# Revit family: CENTUM Doppel-Rollenlager, radial- axial
name_source: partatom
category: HLS-Bauteile
revit_build: Autodesk Revit 2017 (Build: 20190507_1515(x64)
units: mm (PartAtom-declared; Revit-internal decimal feet)

## family parameters
Arbeitsebenenbasiert = Ja
Beim Laden mit Abzugskörper schneiden = Nein
Bemaßung runder Anschluss = Durchmesser verwenden
Gemeinsam genutzt = Ja
Immer vertikal = Nein
Raumberechnungspunkt = Nein
Teiletyp = Normal

## types (117) — shared parameters
Fabrikat = MEFA
Firma = MEFA Befestigungs- und Montagesysteme GmbH
Kurztext1 = Rollenlager doppel radial-axial
Material = Stahl
Materialname = S235
Mengeneinheit = St
Vorgabe-Ansicht = 1219 mm
vpe = 1 St
zero-valued in all types: Sicherheitsfaktor

## per-type parameters (varying)
| type | Artikelnummer | Breite mit Laschen | Doppel-Rollenlager, ra-ax | EAN | Gewicht | Gewicht pro Bauteil | Höhe | Kurztext2 | Langloch | Lasttyp | Lochabstand längs | Lochabstand quer | Länge | Oberflaeche | Schiebeweg | Stärke Material | max. Auflagenbreite | max. zul. Last | min. Auflagenbreite |
| Doppel-Rollenlager, radial- axial  114- 273 DRX003 L= 100, fvz | 150xfa030273 | 232 mm | MEFA Doppel-Rollenlager, radial- axial  114- 273 DRX003 L= 100 | 4250928435460 | 8.62 kg | 8.62 kg | 76 mm | 114 - 273 mm 3 kN 100 mm fsv | 14x27 mm | DRX 003 | 180 mm  [stored 0.590551 ft] | 204 mm | 320 mm  [stored 1.04987 ft] | feuerstückverzinkt | 100 mm | 3 mm  [stored 0.00984252 ft] | 273 mm | 3.00 kN | 114 mm |
| Doppel-Rollenlager, radial- axial  219- 406 DRX005 L= 100, fvz | 150xfa040406 | 244 mm | MEFA Doppel-Rollenlager, radial- axial  219- 406 DRX005 L= 100 | 4250928435477 | 11.26 kg | 11.26 kg | 86 mm | 219 - 406 mm 5 kN 100 mm fsv | 14x27 mm | DRX 005 | 230 mm  [stored 0.754593 ft] | 216 mm  [stored 0.708661 ft] | 370 mm  [stored 1.21391 ft] | feuerstückverzinkt | 100 mm | 4 mm  [stored 0.0131234 ft] | 406 mm | 5.00 kN | 219 mm |
| Doppel-Rollenlager, radial- axial  114- 273 DRX003 L= 100, gvz | 150xga030273 | 232 mm | MEFA Doppel-Rollenlager, radial- axial  114- 273 DRX003 L= 100 | 4250928435859 | 8.26 kg | 8.26 kg | 76 mm | 114 - 273 mm 3 kN 100 mm gvz | 14x27 mm | DRX 003 | 180 mm  [stored 0.590551 ft] | 204 mm | 320 mm  [stored 1.04987 ft] | galvanisch verzinkt | 100 mm | 3 mm  [stored 0.00984252 ft] | 273 mm | 3.00 kN | 114 mm |
| Doppel-Rollenlager, radial- axial  114- 273 DRX003 L= 100, roh | 150xra030273 | 232 mm | MEFA Doppel-Rollenlager, radial- axial  114- 273 DRX003 L= 100 | 4250928436245 | 8.26 kg | 8.26 kg | 76 mm | 114 - 273 mm 3 kN 100 mm roh | 14x27 mm | DRX 003 | 180 mm  [stored 0.590551 ft] | 204 mm | 320 mm  [stored 1.04987 ft] | roh | 100 mm | 3 mm  [stored 0.00984252 ft] | 273 mm | 3.00 kN | 114 mm |
| Doppel-Rollenlager, radial- axial  219- 406 DRX005 L= 100, gvz | 150xga040406 | 244 mm | MEFA Doppel-Rollenlager, radial- axial  219- 406 DRX005 L= 100 | 4250928435866 | 10.83 kg | 10.83 kg | 86 mm | 219 - 406 mm 5 kN 100 mm gvz | 14x27 mm | DRX 005 | 230 mm  [stored 0.754593 ft] | 216 mm  [stored 0.708661 ft] | 370 mm  [stored 1.21391 ft] | galvanisch verzinkt | 100 mm | 4 mm  [stored 0.0131234 ft] | 406 mm | 5.00 kN | 219 mm |
| Doppel-Rollenlager, radial- axial  219- 406 DRX005 L= 100, roh | 150xra040406 | 244 mm | MEFA Doppel-Rollenlager, radial- axial  219- 406 DRX005 L= 100 | 4250928436252 | 10.83 kg | 10.83 kg | 86 mm | 219 - 406 mm 5 kN 100 mm roh | 14x27 mm | DRX 005 | 230 mm  [stored 0.754593 ft] | 216 mm  [stored 0.708661 ft] | 370 mm  [stored 1.21391 ft] | roh | 100 mm | 4 mm  [stored 0.0131234 ft] | 406 mm | 5.00 kN | 219 mm |
| Doppel-Rollenlager, radial- axial  114- 273 DRX003 L= 200, fvz | 150xfb030273 | 232 mm | MEFA Doppel-Rollenlager, radial- axial  114- 273 DRX003 L= 200 | 4250928435590 | 9.85 kg | 9.85 kg | 76 mm | 114 - 273 mm 3 kN 200 mm fsv | 14x27 mm | DRX 003 | 280 mm  [stored 0.918635 ft] | 204 mm | 420 mm  [stored 1.37795 ft] | feuerstückverzinkt | 200 mm | 3 mm  [stored 0.00984252 ft] | 273 mm | 3.00 kN | 114 mm |
| Doppel-Rollenlager, radial- axial  114- 273 DRX003 L= 200, gvz | 150xgb030273 | 232 mm | MEFA Doppel-Rollenlager, radial- axial  114- 273 DRX003 L= 200 | 4250928435989 | 9.10 kg | 9.10 kg | 76 mm | 114 - 273 mm 3 kN 200 mm gvz | 14x27 mm | DRX 003 | 280 mm  [stored 0.918635 ft] | 204 mm | 420 mm  [stored 1.37795 ft] | galvanisch verzinkt | 200 mm | 3 mm  [stored 0.00984252 ft] | 273 mm | 3.00 kN | 114 mm |
| Doppel-Rollenlager, radial- axial  114- 273 DRX003 L= 200, roh | 150xrb030273 | 232 mm | MEFA Doppel-Rollenlager, radial- axial  114- 273 DRX003 L= 200 | 4250928436375 | 9.43 kg | 9.43 kg | 76 mm | 114 - 273 mm 3 kN 200 mm roh | 14x27 mm | DRX 003 | 280 mm  [stored 0.918635 ft] | 204 mm | 420 mm  [stored 1.37795 ft] | roh | 200 mm | 3 mm  [stored 0.00984252 ft] | 273 mm | 3.00 kN | 114 mm |
| Doppel-Rollenlager, radial- axial  114- 273 DRX003 L= 300, fvz | 150xfc030273 | 232 mm | MEFA Doppel-Rollenlager, radial- axial  114- 273 DRX003 L= 300 | 4250928435729 | 11.09 kg | 11.09 kg | 76 mm | 114 - 273 mm 3 kN 300 mm fsv | 14x27 mm | DRX 003 | 380 mm | 204 mm | 520 mm  [stored 1.70604 ft] | feuerstückverzinkt | 300 mm | 3 mm  [stored 0.00984252 ft] | 273 mm | 3.00 kN | 114 mm |
| Doppel-Rollenlager, radial- axial  114- 273 DRX003 L= 300, gvz | 150xgc030273 | 232 mm | MEFA Doppel-Rollenlager, radial- axial  114- 273 DRX003 L= 300 | 4250928436115 | 10.20 kg | 10.20 kg | 76 mm | 114 - 273 mm 3 kN 300 mm gvz | 14x27 mm | DRX 003 | 380 mm | 204 mm | 520 mm  [stored 1.70604 ft] | galvanisch verzinkt | 300 mm | 3 mm  [stored 0.00984252 ft] | 273 mm | 3.00 kN | 114 mm |
| Doppel-Rollenlager, radial- axial  114- 273 DRX003 L= 300, roh | 150xrc030273 | 232 mm | MEFA Doppel-Rollenlager, radial- axial  114- 273 DRX003 L= 300 | 4250928436504 | 10.61 kg | 10.61 kg | 76 mm | 114 - 273 mm 3 kN 300 mm roh | 14x27 mm | DRX 003 | 380 mm | 204 mm | 520 mm  [stored 1.70604 ft] | roh | 300 mm | 3 mm  [stored 0.00984252 ft] | 273 mm | 3.00 kN | 114 mm |
| Doppel-Rollenlager, radial- axial  219- 406 DRX005 L= 200, fvz | 150xfb040406 | 244 mm | MEFA Doppel-Rollenlager, radial- axial  219- 406 DRX005 L= 200 | 4250928435606 | 12.50 kg | 12.50 kg | 86 mm | 219 - 406 mm 5 kN 200 mm fsv | 14x27 mm | DRX 005 | 330 mm | 216 mm  [stored 0.708661 ft] | 470 mm  [stored 1.54199 ft] | feuerstückverzinkt | 200 mm | 4 mm  [stored 0.0131234 ft] | 406 mm | 5.00 kN | 219 mm |
| Doppel-Rollenlager, radial- axial  219- 406 DRX005 L= 200, gvz | 150xgb040406 | 244 mm | MEFA Doppel-Rollenlager, radial- axial  219- 406 DRX005 L= 200 | 4250928435996 | 11.60 kg | 11.60 kg | 86 mm | 219 - 406 mm 5 kN 200 mm gvz | 14x27 mm | DRX 005 | 330 mm | 216 mm  [stored 0.708661 ft] | 470 mm  [stored 1.54199 ft] | galvanisch verzinkt | 200 mm | 4 mm  [stored 0.0131234 ft] | 406 mm | 5.00 kN | 219 mm |
| Doppel-Rollenlager, radial- axial  219- 406 DRX005 L= 200, roh | 150xrb040406 | 244 mm | MEFA Doppel-Rollenlager, radial- axial  219- 406 DRX005 L= 200 | 4250928436382 | 12.00 kg | 12.00 kg | 86 mm | 219 - 406 mm 5 kN 200 mm roh | 14x27 mm | DRX 005 | 330 mm | 216 mm  [stored 0.708661 ft] | 470 mm  [stored 1.54199 ft] | roh | 200 mm | 4 mm  [stored 0.0131234 ft] | 406 mm | 5.00 kN | 219 mm |
| Doppel-Rollenlager, radial- axial  219- 406 DRX005 L= 300, fvz | 150xfc040406 | 244 mm | MEFA Doppel-Rollenlager, radial- axial  219- 406 DRX005 L= 300 | 4250928435736 | 13.74 kg | 13.74 kg | 86 mm | 219 - 406 mm 5 kN 300 mm fsv | 14x27 mm | DRX 005 | 430 mm | 216 mm  [stored 0.708661 ft] | 570 mm  [stored 1.87008 ft] | feuerstückverzinkt | 300 mm | 4 mm  [stored 0.0131234 ft] | 406 mm | 5.00 kN | 219 mm |
| Doppel-Rollenlager, radial- axial  219- 406 DRX005 L= 300, gvz | 150xgc040406 | 244 mm | MEFA Doppel-Rollenlager, radial- axial  219- 406 DRX005 L= 300 | 4250928436122 | 12.70 kg | 12.70 kg | 86 mm | 219 - 406 mm 5 kN 300 mm gvz | 14x27 mm | DRX 005 | 430 mm | 216 mm  [stored 0.708661 ft] | 570 mm  [stored 1.87008 ft] | galvanisch verzinkt | 300 mm | 4 mm  [stored 0.0131234 ft] | 406 mm | 5.00 kN | 219 mm |
| Doppel-Rollenlager, radial- axial  219- 406 DRX005 L= 300, roh | 150xrc040406 | 244 mm | MEFA Doppel-Rollenlager, radial- axial  219- 406 DRX005 L= 300 | 4250928436511 | 13.18 kg | 13.18 kg | 86 mm | 219 - 406 mm 5 kN 300 mm roh | 14x27 mm | DRX 005 | 430 mm | 216 mm  [stored 0.708661 ft] | 570 mm  [stored 1.87008 ft] | roh | 300 mm | 4 mm  [stored 0.0131234 ft] | 406 mm | 5.00 kN | 219 mm |
| Doppel-Rollenlager, radial- axial  323- 660 DRX015 L= 100, fvz | 150xfa050660 | 250 mm | MEFA Doppel-Rollenlager, radial- axial  323- 660 DRX015 L= 100 | 4250928435484 | 18.00 kg | 18.00 kg | 109 mm | 323 - 660 mm 15 kN 100 mm fsv | 14x27 mm | DRX 015 | 345 mm  [stored 1.13189 ft] | 230 mm  [stored 0.754593 ft] | 485 mm  [stored 1.59121 ft] | feuerstückverzinkt | 100 mm | 6 mm  [stored 0.019685 ft] | 660 mm | 15.00 kN | 323 mm |
| Doppel-Rollenlager, radial- axial  323- 660 DRX015 L= 100, gvz | 150xga050660 | 250 mm | MEFA Doppel-Rollenlager, radial- axial  323- 660 DRX015 L= 100 | 4250928435873 | 17.40 kg | 17.40 kg | 109 mm | 323 - 660 mm 15 kN 100 mm gvz | 14x27 mm | DRX 015 | 345 mm  [stored 1.13189 ft] | 230 mm  [stored 0.754593 ft] | 485 mm  [stored 1.59121 ft] | galvanisch verzinkt | 100 mm | 6 mm  [stored 0.019685 ft] | 660 mm | 15.00 kN | 323 mm |
| Doppel-Rollenlager, radial- axial  323- 660 DRX015 L= 100, roh | 150xra050660 | 250 mm | MEFA Doppel-Rollenlager, radial- axial  323- 660 DRX015 L= 100 | 4250928436269 | 17.40 kg | 17.40 kg | 109 mm | 323 - 660 mm 15 kN 100 mm roh | 14x27 mm | DRX 015 | 345 mm  [stored 1.13189 ft] | 230 mm  [stored 0.754593 ft] | 485 mm  [stored 1.59121 ft] | roh | 100 mm | 6 mm  [stored 0.019685 ft] | 660 mm | 15.00 kN | 323 mm |
| Doppel-Rollenlager, radial- axial  323- 660 DRX015 L= 200, fvz | 150xfb050660 | 250 mm | MEFA Doppel-Rollenlager, radial- axial  323- 660 DRX015 L= 200 | 4250928435613 | 19.24 kg | 19.24 kg | 109 mm | 323 - 660 mm 15 kN 200 mm fsv | 14x27 mm | DRX 015 | 445 mm  [stored 1.45997 ft] | 230 mm  [stored 0.754593 ft] | 585 mm  [stored 1.91929 ft] | feuerstückverzinkt | 200 mm | 6 mm  [stored 0.019685 ft] | 660 mm | 15.00 kN | 323 mm |
| Doppel-Rollenlager, radial- axial  323- 660 DRX015 L= 200, gvz | 150xgb050660 | 250 mm | MEFA Doppel-Rollenlager, radial- axial  323- 660 DRX015 L= 200 | 4250928436009 | 18.00 kg | 18.00 kg | 109 mm | 323 - 660 mm 15 kN 200 mm gvz | 14x27 mm | DRX 015 | 445 mm  [stored 1.45997 ft] | 230 mm  [stored 0.754593 ft] | 585 mm  [stored 1.91929 ft] | galvanisch verzinkt | 200 mm | 6 mm  [stored 0.019685 ft] | 660 mm | 15.00 kN | 323 mm |
| Doppel-Rollenlager, radial- axial  323- 660 DRX015 L= 200, roh | 150xrb050660 | 250 mm | MEFA Doppel-Rollenlager, radial- axial  323- 660 DRX015 L= 200 | 4250928436399 | 18.57 kg | 18.57 kg | 109 mm | 323 - 660 mm 15 kN 200 mm roh | 14x27 mm | DRX 015 | 445 mm  [stored 1.45997 ft] | 230 mm  [stored 0.754593 ft] | 585 mm  [stored 1.91929 ft] | roh | 200 mm | 6 mm  [stored 0.019685 ft] | 660 mm | 15.00 kN | 323 mm |
| Doppel-Rollenlager, radial- axial  323- 660 DRX015 L= 300, fvz | 150xfc050660 | 250 mm | MEFA Doppel-Rollenlager, radial- axial  323- 660 DRX015 L= 300 | 4250928435743 | 20.48 kg | 20.48 kg | 109 mm | 323 - 660 mm 15 kN 300 mm fsv | 14x27 mm | DRX 015 | 545 mm  [stored 1.78806 ft] | 230 mm  [stored 0.754593 ft] | 685 mm | feuerstückverzinkt | 300 mm | 6 mm  [stored 0.019685 ft] | 660 mm | 15.00 kN | 323 mm |
| Doppel-Rollenlager, radial- axial  323- 660 DRX015 L= 300, gvz | 150xgc050660 | 250 mm | MEFA Doppel-Rollenlager, radial- axial  323- 660 DRX015 L= 300 | 4250928436139 | 19.10 kg | 19.10 kg | 109 mm | 323 - 660 mm 15 kN 300 mm gvz | 14x27 mm | DRX 015 | 545 mm  [stored 1.78806 ft] | 230 mm  [stored 0.754593 ft] | 685 mm | galvanisch verzinkt | 300 mm | 6 mm  [stored 0.019685 ft] | 660 mm | 15.00 kN | 323 mm |
| Doppel-Rollenlager, radial- axial  323- 660 DRX015 L= 300, roh | 150xrc050660 | 250 mm | MEFA Doppel-Rollenlager, radial- axial  323- 660 DRX015 L= 300 | 4250928436528 | 19.74 kg | 19.74 kg | 109 mm | 323 - 660 mm 15 kN 300 mm roh | 14x27 mm | DRX 015 | 545 mm  [stored 1.78806 ft] | 230 mm  [stored 0.754593 ft] | 685 mm | roh | 300 mm | 6 mm  [stored 0.019685 ft] | 660 mm | 15.00 kN | 323 mm |
| Doppel-Rollenlager, radial- axial  323- 660 DRX025 L= 100, fvz | 150xfa060660 | 250 mm | MEFA Doppel-Rollenlager, radial- axial  323- 660 DRX025 L= 100 | 4250928435491 | 18.07 kg | 18.07 kg | 109 mm | 323 - 660 mm 25 kN 100 mm fsv | 14x27 mm | DRX 025 | 345 mm  [stored 1.13189 ft] | 230 mm  [stored 0.754593 ft] | 485 mm  [stored 1.59121 ft] | feuerstückverzinkt | 100 mm | 6 mm  [stored 0.019685 ft] | 660 mm | 25.00 kN | 323 mm |
| Doppel-Rollenlager, radial- axial  323- 660 DRX025 L= 100, gvz | 150xga060660 | 250 mm | MEFA Doppel-Rollenlager, radial- axial  323- 660 DRX025 L= 100 | 4250928435880 | 16.90 kg | 16.90 kg | 109 mm | 323 - 660 mm 25 kN 100 mm gvz | 14x27 mm | DRX 025 | 345 mm  [stored 1.13189 ft] | 230 mm  [stored 0.754593 ft] | 485 mm  [stored 1.59121 ft] | galvanisch verzinkt | 100 mm | 6 mm  [stored 0.019685 ft] | 660 mm | 25.00 kN | 323 mm |
| Doppel-Rollenlager, radial- axial  323- 660 DRX025 L= 100, roh | 150xra060660 | 250 mm | MEFA Doppel-Rollenlager, radial- axial  323- 660 DRX025 L= 100 | 4250928436276 | 17.46 kg | 17.46 kg | 109 mm | 323 - 660 mm 25 kN 100 mm roh | 14x27 mm | DRX 025 | 345 mm  [stored 1.13189 ft] | 230 mm  [stored 0.754593 ft] | 485 mm  [stored 1.59121 ft] | roh | 100 mm | 6 mm  [stored 0.019685 ft] | 660 mm | 25.00 kN | 323 mm |
| Doppel-Rollenlager, radial- axial  323- 660 DRX025 L= 200, fvz | 150xfb060660 | 250 mm | MEFA Doppel-Rollenlager, radial- axial  323- 660 DRX025 L= 200 | 4250928435620 | 19.30 kg | 19.30 kg | 109 mm | 323 - 660 mm 25 kN 200 mm fsv | 14x27 mm | DRX 025 | 445 mm  [stored 1.45997 ft] | 230 mm  [stored 0.754593 ft] | 585 mm  [stored 1.91929 ft] | feuerstückverzinkt | 200 mm | 6 mm  [stored 0.019685 ft] | 660 mm | 25.00 kN | 323 mm |
| Doppel-Rollenlager, radial- axial  323- 660 DRX025 L= 200, gvz | 150xgb060660 | 250 mm | MEFA Doppel-Rollenlager, radial- axial  323- 660 DRX025 L= 200 | 4250928436016 | 18.10 kg | 18.10 kg | 109 mm | 323 - 660 mm 25 kN 200 mm gvz | 14x27 mm | DRX 025 | 445 mm  [stored 1.45997 ft] | 230 mm  [stored 0.754593 ft] | 585 mm  [stored 1.91929 ft] | galvanisch verzinkt | 200 mm | 6 mm  [stored 0.019685 ft] | 660 mm | 25.00 kN | 323 mm |
| Doppel-Rollenlager, radial- axial  323- 660 DRX025 L= 200, roh | 150xrb060660 | 250 mm | MEFA Doppel-Rollenlager, radial- axial  323- 660 DRX025 L= 200 | 4250928436405 | 18.63 kg | 18.63 kg | 109 mm | 323 - 660 mm 25 kN 200 mm roh | 14x27 mm | DRX 025 | 445 mm  [stored 1.45997 ft] | 230 mm  [stored 0.754593 ft] | 585 mm  [stored 1.91929 ft] | roh | 200 mm | 6 mm  [stored 0.019685 ft] | 660 mm | 25.00 kN | 323 mm |
| Doppel-Rollenlager, radial- axial  323- 660 DRX025 L= 300, fvz | 150xfc060660 | 250 mm | MEFA Doppel-Rollenlager, radial- axial  323- 660 DRX025 L= 300 | 4250928435750 | 20.54 kg | 20.54 kg | 109 mm | 323 - 660 mm 25 kN 300 mm fsv | 14x27 mm | DRX 025 | 545 mm  [stored 1.78806 ft] | 230 mm  [stored 0.754593 ft] | 685 mm | feuerstückverzinkt | 300 mm | 6 mm  [stored 0.019685 ft] | 660 mm | 25.00 kN | 323 mm |
| Doppel-Rollenlager, radial- axial  323- 660 DRX025 L= 300, gvz | 150xgc060660 | 250 mm | MEFA Doppel-Rollenlager, radial- axial  323- 660 DRX025 L= 300 | 4250928436146 | 19.81 kg | 19.81 kg | 109 mm | 323 - 660 mm 25 kN 300 mm gvz | 14x27 mm | DRX 025 | 545 mm  [stored 1.78806 ft] | 230 mm  [stored 0.754593 ft] | 685 mm | galvanisch verzinkt | 300 mm | 6 mm  [stored 0.019685 ft] | 660 mm | 25.00 kN | 323 mm |
| Doppel-Rollenlager, radial- axial  323- 660 DRX025 L= 300, roh | 150xrc060660 | 258 mm | MEFA Doppel-Rollenlager, radial- axial  323- 660 DRX025 L= 300 | 4250928436535 | 19.81 kg | 19.81 kg | 109 mm | 323 - 660 mm 25 kN 300 mm roh | 14x27 mm | DRX 025 | 545 mm  [stored 1.78806 ft] | 230 mm  [stored 0.754593 ft] | 685 mm | roh | 300 mm | 6 mm  [stored 0.019685 ft] | 660 mm | 25.00 kN | 323 mm |
| Doppel-Rollenlager, radial- axial  508- 965 DRX025 L= 100, fvz | 150xfa060965 | 322 mm | MEFA Doppel-Rollenlager, radial- axial  508- 965 DRX025 L= 100 | 4250928435507 | 35.16 kg | 35.16 kg | 145 mm | 508 - 965 mm 25 kN 100 mm fsv | 18x36 mm | DRX 025 | 490 mm  [stored 1.60761 ft] | 286 mm | 630 mm  [stored 2.06693 ft] | feuerstückverzinkt | 100 mm | 6 mm  [stored 0.019685 ft] | 965 mm | 25.00 kN | 508 mm |
| Doppel-Rollenlager, radial- axial  508- 965 DRX025 L= 100, gvz | 150xga060965 | 322 mm | MEFA Doppel-Rollenlager, radial- axial  508- 965 DRX025 L= 100 | 4250928435897 | 34.17 kg | 34.17 kg | 145 mm | 508 - 965 mm 25 kN 100 mm gvz | 18x36 mm | DRX 025 | 490 mm  [stored 1.60761 ft] | 286 mm | 630 mm  [stored 2.06693 ft] | galvanisch verzinkt | 100 mm | 6 mm  [stored 0.019685 ft] | 965 mm | 25.00 kN | 508 mm |
| Doppel-Rollenlager, radial- axial  508- 965 DRX025 L= 100, roh | 150xra060965 | 322 mm | MEFA Doppel-Rollenlager, radial- axial  508- 965 DRX025 L= 100 | 4250928436283 | 34.17 kg | 34.17 kg | 145 mm | 508 - 965 mm 25 kN 100 mm roh | 18x36 mm | DRX 025 | 490 mm  [stored 1.60761 ft] | 286 mm | 630 mm  [stored 2.06693 ft] | roh | 100 mm | 6 mm  [stored 0.019685 ft] | 965 mm | 25.00 kN | 508 mm |
| Doppel-Rollenlager, radial- axial  508- 965 DRX025 L= 200, fvz | 150xfb060965 | 322 mm | MEFA Doppel-Rollenlager, radial- axial  508- 965 DRX025 L= 200 | 4250928435637 | 36.73 kg | 36.73 kg | 145 mm | 508 - 965 mm 25 kN 200 mm fsv | 18x36 mm | DRX 025 | 590 mm  [stored 1.9357 ft] | 286 mm | 730 mm | feuerstückverzinkt | 200 mm | 6 mm  [stored 0.019685 ft] | 965 mm | 25.00 kN | 508 mm |
| Doppel-Rollenlager, radial- axial  508- 965 DRX025 L= 200, gvz | 150xgb060965 | 322 mm | MEFA Doppel-Rollenlager, radial- axial  508- 965 DRX025 L= 200 | 4250928436023 | 34.70 kg | 34.70 kg | 145 mm | 508 - 965 mm 25 kN 200 mm gvz | 18x36 mm | DRX 025 | 590 mm  [stored 1.9357 ft] | 286 mm | 730 mm | galvanisch verzinkt | 200 mm | 6 mm  [stored 0.019685 ft] | 965 mm | 25.00 kN | 508 mm |
| Doppel-Rollenlager, radial- axial  508- 965 DRX025 L= 200, roh | 150xrb060965 | 322 mm | MEFA Doppel-Rollenlager, radial- axial  508- 965 DRX025 L= 200 | 4250928436412 | 35.66 kg | 35.66 kg | 145 mm | 508 - 965 mm 25 kN 200 mm roh | 18x36 mm | DRX 025 | 590 mm  [stored 1.9357 ft] | 286 mm | 730 mm | roh | 200 mm | 6 mm  [stored 0.019685 ft] | 965 mm | 25.00 kN | 508 mm |
| Doppel-Rollenlager, radial- axial  508- 965 DRX025 L= 300, fvz | 150xfc060965 | 322 mm | MEFA Doppel-Rollenlager, radial- axial  508- 965 DRX025 L= 300 | 4250928435767 | 38.30 kg | 38.30 kg | 145 mm | 508 - 965 mm 25 kN 300 mm fsv | 18x36 mm | DRX 025 | 690 mm | 286 mm | 830 mm | feuerstückverzinkt | 300 mm | 6 mm  [stored 0.019685 ft] | 965 mm | 25.00 kN | 508 mm |
| Doppel-Rollenlager, radial- axial  508- 965 DRX025 L= 300, gvz | 150xgc060965 | 322 mm | MEFA Doppel-Rollenlager, radial- axial  508- 965 DRX025 L= 300 | 4250928436153 | 36.10 kg | 36.10 kg | 145 mm | 508 - 965 mm 25 kN 300 mm gvz | 18x36 mm | DRX 025 | 690 mm | 286 mm | 830 mm | galvanisch verzinkt | 300 mm | 6 mm  [stored 0.019685 ft] | 965 mm | 25.00 kN | 508 mm |
| Doppel-Rollenlager, radial- axial  508- 965 DRX025 L= 300, roh | 150xrc060965 | 322 mm | MEFA Doppel-Rollenlager, radial- axial  508- 965 DRX025 L= 300 | 4250928436542 | 37.15 kg | 37.15 kg | 145 mm | 508 - 965 mm 25 kN 300 mm roh | 18x36 mm | DRX 025 | 690 mm | 286 mm | 830 mm | roh | 300 mm | 6 mm  [stored 0.019685 ft] | 965 mm | 25.00 kN | 508 mm |
| Doppel-Rollenlager, radial- axial  508- 965 DRX050 L= 100, fvz | 150xfa080965 | 328 mm | MEFA Doppel-Rollenlager, radial- axial  508- 965 DRX050 L= 100 | 4250928435514 | 37.10 kg | 37.10 kg | 145 mm | 508 - 965 mm 50 kN 100 mm fsv | 18x36 mm | DRX 050 | 490 mm  [stored 1.60761 ft] | 292 mm  [stored 0.958005 ft] | 630 mm  [stored 2.06693 ft] | feuerstückverzinkt | 100 mm | 6 mm  [stored 0.019685 ft] | 965 mm | 50.00 kN | 508 mm |
| Doppel-Rollenlager, radial- axial  508- 965 DRX050 L= 100, gvz | 150xga080965 | 328 mm | MEFA Doppel-Rollenlager, radial- axial  508- 965 DRX050 L= 100 | 4250928435903 | 36.10 kg | 36.10 kg | 145 mm | 508 - 965 mm 50 kN 100 mm gvz | 18x36 mm | DRX 050 | 490 mm  [stored 1.60761 ft] | 292 mm  [stored 0.958005 ft] | 630 mm  [stored 2.06693 ft] | galvanisch verzinkt | 100 mm | 6 mm  [stored 0.019685 ft] | 965 mm | 50.00 kN | 508 mm |
| Doppel-Rollenlager, radial- axial  508- 965 DRX050 L= 200, fvz | 150xfb080965 | 328 mm | MEFA Doppel-Rollenlager, radial- axial  508- 965 DRX050 L= 200 | 4250928435644 | 38.67 kg | 38.67 kg | 145 mm | 508 - 965 mm 50 kN 200 mm fsv | 18x36 mm | DRX 050 | 590 mm  [stored 1.9357 ft] | 292 mm  [stored 0.958005 ft] | 730 mm | feuerstückverzinkt | 200 mm | 6 mm  [stored 0.019685 ft] | 965 mm | 50.00 kN | 508 mm |
| Doppel-Rollenlager, radial- axial  508- 965 DRX050 L= 100, roh | 150xra080965 | 328 mm | MEFA Doppel-Rollenlager, radial- axial  508- 965 DRX050 L= 100 | 4250928436290 | 36.10 kg | 36.10 kg | 145 mm | 508 - 965 mm 50 kN 100 mm roh | 18x36 mm | DRX 050 | 490 mm  [stored 1.60761 ft] | 292 mm  [stored 0.958005 ft] | 630 mm  [stored 2.06693 ft] | roh | 100 mm | 6 mm  [stored 0.019685 ft] | 965 mm | 50.00 kN | 508 mm |
| Doppel-Rollenlager, radial- axial  508- 965 DRX050 L= 200, gvz | 150xgb080965 | 328 mm | MEFA Doppel-Rollenlager, radial- axial  508- 965 DRX050 L= 200 | 4250928436030 | 36.50 kg | 36.50 kg | 145 mm | 508 - 965 mm 50 kN 200 mm gvz | 18x36 mm | DRX 050 | 590 mm  [stored 1.9357 ft] | 292 mm  [stored 0.958005 ft] | 730 mm | galvanisch verzinkt | 200 mm | 6 mm  [stored 0.019685 ft] | 965 mm | 50.00 kN | 508 mm |
| Doppel-Rollenlager, radial- axial  508- 965 DRX050 L= 200, roh | 150xrb080965 | 328 mm | MEFA Doppel-Rollenlager, radial- axial  508- 965 DRX050 L= 200 | 4250928436429 | 37.59 kg | 37.59 kg | 145 mm | 508 - 965 mm 50 kN 200 mm roh | 18x36 mm | DRX 050 | 590 mm  [stored 1.9357 ft] | 292 mm  [stored 0.958005 ft] | 730 mm | roh | 200 mm | 6 mm  [stored 0.019685 ft] | 965 mm | 50.00 kN | 508 mm |
| Doppel-Rollenlager, radial- axial  508- 965 DRX050 L= 300, fvz | 150xfc080965 | 328 mm | MEFA Doppel-Rollenlager, radial- axial  508- 965 DRX050 L= 300 | 4250928435774 | 40.23 kg | 40.23 kg | 145 mm | 508 - 965 mm 50 kN 300 mm fsv | 18x36 mm | DRX 050 | 690 mm | 292 mm  [stored 0.958005 ft] | 830 mm | feuerstückverzinkt | 300 mm | 6 mm  [stored 0.019685 ft] | 965 mm | 50.00 kN | 508 mm |
| Doppel-Rollenlager, radial- axial  508- 965 DRX050 L= 300, gvz | 150xgc080965 | 328 mm | MEFA Doppel-Rollenlager, radial- axial  508- 965 DRX050 L= 300 | 4250928436160 | 38.00 kg | 38.00 kg | 145 mm | 508 - 965 mm 50 kN 300 mm gvz | 18x36 mm | DRX 050 | 690 mm | 292 mm  [stored 0.958005 ft] | 830 mm | galvanisch verzinkt | 300 mm | 6 mm  [stored 0.019685 ft] | 965 mm | 50.00 kN | 508 mm |
| Doppel-Rollenlager, radial- axial  508- 965 DRX050 L= 300, roh | 150xrc080965 | 328 mm | MEFA Doppel-Rollenlager, radial- axial  508- 965 DRX050 L= 300 | 4250928436559 | 39.08 kg | 39.08 kg | 145 mm | 508 - 965 mm 50 kN 300 mm roh | 18x36 mm | DRX 050 | 690 mm | 292 mm  [stored 0.958005 ft] | 830 mm | roh | 300 mm | 8 mm  [stored 0.0262467 ft] | 965 mm | 50.00 kN | 508 mm |
| Doppel-Rollenlager, radial- axial  508- 965 DRX100 L= 100, fvz | 150xfa100965 | 332 mm | MEFA Doppel-Rollenlager, radial- axial  508- 965 DRX100 L= 100 | 4250928435538 | 39.14 kg | 39.14 kg | 145 mm | 508 - 965 mm 100 kN 100 mm fsv | 18x36 mm | DRX 100 | 490 mm  [stored 1.60761 ft] | 296 mm  [stored 0.971129 ft] | 630 mm  [stored 2.06693 ft] | feuerstückverzinkt | 100 mm | 6 mm  [stored 0.019685 ft] | 965 mm | 100.00 kN | 508 mm |
| Doppel-Rollenlager, radial- axial  508- 965 DRX100 L= 100, gvz | 150xga100965 | 332 mm | MEFA Doppel-Rollenlager, radial- axial  508- 965 DRX100 L= 100 | 4250928435927 | 38.14 kg | 38.14 kg | 145 mm | 508 - 965 mm 100 kN 100 mm gvz | 18x36 mm | DRX 100 | 490 mm  [stored 1.60761 ft] | 296 mm  [stored 0.971129 ft] | 630 mm  [stored 2.06693 ft] | galvanisch verzinkt | 100 mm | 6 mm  [stored 0.019685 ft] | 965 mm | 100.00 kN | 508 mm |
| Doppel-Rollenlager, radial- axial  508- 965 DRX100 L= 100, roh | 150xra100965 | 332 mm | MEFA Doppel-Rollenlager, radial- axial  508- 965 DRX100 L= 100 | 4250928436313 | 38.14 kg | 38.14 kg | 145 mm | 508 - 965 mm 100 kN 100 mm roh | 18x36 mm | DRX 100 | 490 mm  [stored 1.60761 ft] | 296 mm  [stored 0.971129 ft] | 630 mm  [stored 2.06693 ft] | roh | 100 mm | 10 mm  [stored 0.0328084 ft] | 965 mm | 100.00 kN | 508 mm |
| Doppel-Rollenlager, radial- axial  508- 965 DRX100 L= 200, fvz | 150xfb100965 | 332 mm | MEFA Doppel-Rollenlager, radial- axial  508- 965 DRX100 L= 200 | 4250928435668 | 40.71 kg | 40.71 kg | 145 mm | 508 - 965 mm 100 kN 200 mm fsv | 18x36 mm | DRX 100 | 590 mm  [stored 1.9357 ft] | 296 mm  [stored 0.971129 ft] | 730 mm | feuerstückverzinkt | 200 mm | 6 mm  [stored 0.019685 ft] | 965 mm | 100.00 kN | 508 mm |
| Doppel-Rollenlager, radial- axial  508- 965 DRX100 L= 200, gvz | 150xgb100965 | 332 mm | MEFA Doppel-Rollenlager, radial- axial  508- 965 DRX100 L= 200 | 4250928436054 | 38.50 kg | 38.50 kg | 145 mm | 508 - 965 mm 100 kN 200 mm gvz | 18x36 mm | DRX 100 | 590 mm  [stored 1.9357 ft] | 296 mm  [stored 0.971129 ft] | 730 mm | galvanisch verzinkt | 200 mm | 6 mm  [stored 0.019685 ft] | 965 mm | 100.00 kN | 508 mm |
| Doppel-Rollenlager, radial- axial  508- 965 DRX100 L= 200, roh | 150xrb100965 | 332 mm | MEFA Doppel-Rollenlager, radial- axial  508- 965 DRX100 L= 200 | 4250928436443 | 39.63 kg | 39.63 kg | 145 mm | 508 - 965 mm 100 kN 200 mm roh | 18x36 mm | DRX 100 | 590 mm  [stored 1.9357 ft] | 296 mm  [stored 0.971129 ft] | 730 mm | roh | 200 mm | 6 mm  [stored 0.019685 ft] | 965 mm | 100.00 kN | 508 mm |
| Doppel-Rollenlager, radial- axial  508- 965 DRX100 L= 300, fvz | 150xfc100965 | 332 mm | MEFA Doppel-Rollenlager, radial- axial  508- 965 DRX100 L= 300 | 4250928435798 | 42.28 kg | 42.28 kg | 145 mm | 508 - 965 mm 100 kN 300 mm fsv | 18x36 mm | DRX 100 | 690 mm | 296 mm  [stored 0.971129 ft] | 830 mm | feuerstückverzinkt | 300 mm | 6 mm  [stored 0.019685 ft] | 965 mm | 100.00 kN | 508 mm |
| Doppel-Rollenlager, radial- axial  508- 965 DRX100 L= 300, gvz | 150xgc100965 | 332 mm | MEFA Doppel-Rollenlager, radial- axial  508- 965 DRX100 L= 300 | 4250928436184 | 39.90 kg | 39.90 kg | 145 mm | 508 - 965 mm 100 kN 300 mm gvz | 18x36 mm | DRX 100 | 690 mm | 296 mm  [stored 0.971129 ft] | 830 mm | galvanisch verzinkt | 300 mm | 6 mm  [stored 0.019685 ft] | 965 mm | 100.00 kN | 508 mm |
| Doppel-Rollenlager, radial- axial  508- 965 DRX100 L= 300, roh | 150xrc100965 | 332 mm | MEFA Doppel-Rollenlager, radial- axial  508- 965 DRX100 L= 300 | 4250928436573 | 41.12 kg | 41.12 kg | 145 mm | 508 - 965 mm 100 kN 300 mm roh | 18x36 mm | DRX 100 | 690 mm | 296 mm  [stored 0.971129 ft] | 830 mm | roh | 300 mm | 6 mm  [stored 0.019685 ft] | 965 mm | 100.00 kN | 508 mm |
| Doppel-Rollenlager, radial- axial  813-1350 DRX050 L= 100, fvz | 150xfa081350 | 386 mm | MEFA Doppel-Rollenlager, radial- axial  813-1350 DRX050 L= 100 | 4250928435521 | 73.64 kg | 73.64 kg | 195 mm | 813 - 1.350 mm 50 kN 100 mm fsv | 23x46 mm | DRX 050 | 645 mm  [stored 2.11614 ft] | 340 mm  [stored 1.11549 ft] | 805 mm | feuerstückverzinkt | 100 mm | 12 mm  [stored 0.0393701 ft] | 1.350 mm | 50.00 kN | 813 mm |
| Doppel-Rollenlager, radial- axial  813-1350 DRX050 L= 100, gvz | 150xga081350 | 386 mm | MEFA Doppel-Rollenlager, radial- axial  813-1350 DRX050 L= 100 | 4250928435910 | 72.10 kg | 72.10 kg | 195 mm | 813 - 1.350 mm 50 kN 100 mm gvz | 23x46 mm | DRX 050 | 645 mm  [stored 2.11614 ft] | 340 mm  [stored 1.11549 ft] | 805 mm | galvanisch verzinkt | 100 mm | 12 mm  [stored 0.0393701 ft] | 1.350 mm | 50.00 kN | 813 mm |
| Doppel-Rollenlager, radial- axial  813-1350 DRX050 L= 100, roh | 150xra081350 | 386 mm | MEFA Doppel-Rollenlager, radial- axial  813-1350 DRX050 L= 100 | 4250928436306 | 72.10 kg | 72.10 kg | 195 mm | 813 - 1.350 mm 50 kN 100 mm roh | 23x46 mm | DRX 050 | 645 mm  [stored 2.11614 ft] | 340 mm  [stored 1.11549 ft] | 805 mm | roh | 100 mm | 12 mm  [stored 0.0393701 ft] | 1.350 mm | 50.00 kN | 813 mm |
| Doppel-Rollenlager, radial- axial  813-1350 DRX050 L= 200, fvz | 150xfb081350 | 386 mm | MEFA Doppel-Rollenlager, radial- axial  813-1350 DRX050 L= 200 | 4250928435651 | 75.20 kg | 75.20 kg | 195 mm | 813 - 1.350 mm 50 kN 200 mm fsv | 23x46 mm | DRX 050 | 745 mm | 340 mm  [stored 1.11549 ft] | 905 mm | feuerstückverzinkt | 200 mm | 12 mm  [stored 0.0393701 ft] | 1.350 mm | 50.00 kN | 813 mm |
| Doppel-Rollenlager, radial- axial  813-1350 DRX050 L= 200, gvz | 150xgb081350 | 386 mm | MEFA Doppel-Rollenlager, radial- axial  813-1350 DRX050 L= 200 | 4250928436047 | 71.80 kg | 71.80 kg | 195 mm | 813 - 1.350 mm 50 kN 200 mm gvz | 23x46 mm | DRX 050 | 745 mm | 340 mm  [stored 1.11549 ft] | 905 mm | galvanisch verzinkt | 200 mm | 12 mm  [stored 0.0393701 ft] | 1.350 mm | 50.00 kN | 813 mm |
| Doppel-Rollenlager, radial- axial  813-1350 DRX050 L= 200, roh | 150xrb081350 | 386 mm | MEFA Doppel-Rollenlager, radial- axial  813-1350 DRX050 L= 200 | 4250928436436 | 73.59 kg | 73.59 kg | 195 mm | 813 - 1.350 mm 50 kN 200 mm roh | 23x46 mm | DRX 050 | 745 mm | 340 mm  [stored 1.11549 ft] | 905 mm | roh | 200 mm | 8 mm  [stored 0.0262467 ft] | 1.350 mm | 50.00 kN | 813 mm |
| Doppel-Rollenlager, radial- axial  813-1350 DRX050 L= 300, fvz | 150xfc081350 | 386 mm | MEFA Doppel-Rollenlager, radial- axial  813-1350 DRX050 L= 300 | 4250928435781 | 76.77 kg | 76.77 kg | 195 mm | 813 - 1.350 mm 50 kN 300 mm fsv | 23x46 mm | DRX 050 | 845 mm | 340 mm  [stored 1.11549 ft] | 1005 mm | feuerstückverzinkt | 300 mm | 12 mm  [stored 0.0393701 ft] | 1.350 mm | 50.00 kN | 813 mm |
| Doppel-Rollenlager, radial- axial  813-1350 DRX050 L= 300, gvz | 150xgc081350 | 386 mm | MEFA Doppel-Rollenlager, radial- axial  813-1350 DRX050 L= 300 | 4250928436177 | 73.30 kg | 73.30 kg | 195 mm | 813 - 1.350 mm 50 kN 300 mm gvz | 23x46 mm | DRX 050 | 845 mm | 340 mm  [stored 1.11549 ft] | 1005 mm | galvanisch verzinkt | 300 mm | 12 mm  [stored 0.0393701 ft] | 1.350 mm | 50.00 kN | 813 mm |
| Doppel-Rollenlager, radial- axial  813-1350 DRX050 L= 300, roh | 150xrc081350 | 386 mm | MEFA Doppel-Rollenlager, radial- axial  813-1350 DRX050 L= 300 | 4250928436566 | 75.08 kg | 75.08 kg | 195 mm | 813 - 1.350 mm 50 kN 300 mm roh | 23x46 mm | DRX 050 | 845 mm | 340 mm  [stored 1.11549 ft] | 1005 mm | roh | 300 mm | 8 mm  [stored 0.0262467 ft] | 1.350 mm | 50.00 kN | 813 mm |
| Doppel-Rollenlager, radial- axial  813-1350 DRX100 L= 100, fvz | 150xfa101350 | 390 mm | MEFA Doppel-Rollenlager, radial- axial  813-1350 DRX100 L= 100 | 4250928435545 | 77.52 kg | 77.52 kg | 195 mm | 813 - 1.350 mm 100 kN 100 mm fsv | 23x46 mm | DRX 100 | 645 mm  [stored 2.11614 ft] | 344 mm  [stored 1.12861 ft] | 805 mm | feuerstückverzinkt | 100 mm | 12 mm  [stored 0.0393701 ft] | 1.350 mm | 100.00 kN | 813 mm |
| Doppel-Rollenlager, radial- axial  813-1350 DRX100 L= 100, gvz | 150xga101350 | 390 mm | MEFA Doppel-Rollenlager, radial- axial  813-1350 DRX100 L= 100 | 4250928435934 | 74.10 kg | 74.10 kg | 195 mm | 813 - 1.350 mm 100 kN 100 mm gvz | 23x46 mm | DRX 100 | 645 mm  [stored 2.11614 ft] | 344 mm  [stored 1.12861 ft] | 805 mm | galvanisch verzinkt | 100 mm | 12 mm  [stored 0.0393701 ft] | 1.350 mm | 100.00 kN | 813 mm |
| Doppel-Rollenlager, radial- axial  813-1350 DRX100 L= 100, roh | 150xra101350 | 390 mm | MEFA Doppel-Rollenlager, radial- axial  813-1350 DRX100 L= 100 | 4250928436320 | 75.98 kg | 75.98 kg | 195 mm | 813 - 1.350 mm 100 kN 100 mm roh | 23x46 mm | DRX 100 | 645 mm  [stored 2.11614 ft] | 344 mm  [stored 1.12861 ft] | 805 mm | roh | 100 mm | 8 mm  [stored 0.0262467 ft] | 1.350 mm | 100.00 kN | 813 mm |
| Doppel-Rollenlager, radial- axial  813-1350 DRX100 L= 200, fvz | 150xfb101350 | 390 mm | MEFA Doppel-Rollenlager, radial- axial  813-1350 DRX100 L= 200 | 4250928435675 | 79.08 kg | 79.08 kg | 195 mm | 813 - 1.350 mm 100 kN 200 mm fsv | 23x46 mm | DRX 100 | 745 mm | 344 mm  [stored 1.12861 ft] | 905 mm | feuerstückverzinkt | 200 mm | 12 mm  [stored 0.0393701 ft] | 1.350 mm | 100.00 kN | 813 mm |
| Doppel-Rollenlager, radial- axial  813-1350 DRX100 L= 200, gvz | 150xgb101350 | 390 mm | MEFA Doppel-Rollenlager, radial- axial  813-1350 DRX100 L= 200 | 4250928436061 | 75.60 kg | 75.60 kg | 195 mm | 813 - 1.350 mm 100 kN 200 mm gvz | 23x46 mm | DRX 100 | 745 mm | 344 mm  [stored 1.12861 ft] | 905 mm | galvanisch verzinkt | 200 mm | 12 mm  [stored 0.0393701 ft] | 1.350 mm | 100.00 kN | 813 mm |
| Doppel-Rollenlager, radial- axial  813-1350 DRX100 L= 200, roh | 150xrb101350 | 390 mm | MEFA Doppel-Rollenlager, radial- axial  813-1350 DRX100 L= 200 | 4250928436450 | 77.46 kg | 77.46 kg | 195 mm | 813 - 1.350 mm 100 kN 200 mm roh | 23x46 mm | DRX 100 | 745 mm | 344 mm  [stored 1.12861 ft] | 905 mm | roh | 200 mm | 8 mm  [stored 0.0262467 ft] | 1.350 mm | 100.00 kN | 813 mm |
| Doppel-Rollenlager, radial- axial  813-1350 DRX100 L= 300, fvz | 150xfc101350 | 390 mm | MEFA Doppel-Rollenlager, radial- axial  813-1350 DRX100 L= 300 | 4250928435804 | 80.65 kg | 80.65 kg | 195 mm | 813 - 1.350 mm 100 kN 300 mm fsv | 23x46 mm | DRX 100 | 845 mm | 344 mm  [stored 1.12861 ft] | 1005 mm | feuerstückverzinkt | 300 mm | 12 mm  [stored 0.0393701 ft] | 1.350 mm | 100.00 kN | 813 mm |
| Doppel-Rollenlager, radial- axial  813-1350 DRX100 L= 300, gvz | 150xgc101350 | 390 mm | MEFA Doppel-Rollenlager, radial- axial  813-1350 DRX100 L= 300 | 4250928436191 | 77.00 kg | 77.00 kg | 195 mm | 813 - 1.350 mm 100 kN 300 mm gvz | 23x46 mm | DRX 100 | 845 mm | 344 mm  [stored 1.12861 ft] | 1005 mm | galvanisch verzinkt | 300 mm | 12 mm  [stored 0.0393701 ft] | 1.350 mm | 100.00 kN | 813 mm |
| Doppel-Rollenlager, radial- axial  813-1350 DRX100 L= 300, roh | 150xrc101350 | 390 mm | MEFA Doppel-Rollenlager, radial- axial  813-1350 DRX100 L= 300 | 4250928436580 | 78.96 kg | 78.96 kg | 195 mm | 813 - 1.350 mm 100 kN 300 mm roh | 23x46 mm | DRX 100 | 845 mm | 344 mm  [stored 1.12861 ft] | 1005 mm | roh | 300 mm | 8 mm  [stored 0.0262467 ft] | 1.350 mm | 100.00 kN | 813 mm |
| Doppel-Rollenlager, radial- axial  813-1350 DRX200 L= 100, fvz | 150xfa121350 | 394 mm | MEFA Doppel-Rollenlager, radial- axial  813-1350 DRX200 L= 100 | 4250928435569 | 81.50 kg | 81.50 kg | 195 mm | 813 - 1.350 mm 200 kN 100 mm fsv | 23x46 mm | DRX 200 | 645 mm  [stored 2.11614 ft] | 348 mm  [stored 1.14173 ft] | 805 mm | feuerstückverzinkt | 100 mm | 12 mm  [stored 0.0393701 ft] | 1.350 mm | 200.00 kN | 813 mm |
| Doppel-Rollenlager, radial- axial  813-1350 DRX200 L= 100, gvz | 150xga121350 | 394 mm | MEFA Doppel-Rollenlager, radial- axial  813-1350 DRX200 L= 100 | 4250928435958 | 78.00 kg | 78.00 kg | 195 mm | 813 - 1.350 mm 200 kN 100 mm gvz | 23x46 mm | DRX 200 | 645 mm  [stored 2.11614 ft] | 348 mm  [stored 1.14173 ft] | 805 mm | galvanisch verzinkt | 100 mm | 12 mm  [stored 0.0393701 ft] | 1.350 mm | 200.00 kN | 813 mm |
| Doppel-Rollenlager, radial- axial  813-1350 DRX200 L= 100, roh | 150xra121350 | 394 mm | MEFA Doppel-Rollenlager, radial- axial  813-1350 DRX200 L= 100 | 4250928436344 | 79.97 kg | 79.97 kg | 195 mm | 813 - 1.350 mm 200 kN 100 mm roh | 23x46 mm | DRX 200 | 645 mm  [stored 2.11614 ft] | 348 mm  [stored 1.14173 ft] | 805 mm | roh | 100 mm | 8 mm  [stored 0.0262467 ft] | 1.350 mm | 200.00 kN | 813 mm |
| Doppel-Rollenlager, radial- axial  813-1350 DRX200 L= 200, fvz | 150xfb121350 | 394 mm | MEFA Doppel-Rollenlager, radial- axial  813-1350 DRX200 L= 200 | 4250928435699 | 83.07 kg | 83.07 kg | 195 mm | 813 - 1.350 mm 200 kN 200 mm fsv | 23x46 mm | DRX 200 | 745 mm | 348 mm  [stored 1.14173 ft] | 905 mm | feuerstückverzinkt | 200 mm | 12 mm  [stored 0.0393701 ft] | 1.350 mm | 200.00 kN | 813 mm |
| Doppel-Rollenlager, radial- axial  813-1350 DRX200 L= 200, gvz | 150xgb121350 | 394 mm | MEFA Doppel-Rollenlager, radial- axial  813-1350 DRX200 L= 200 | 4250928436085 | 79.40 kg | 79.40 kg | 195 mm | 813 - 1.350 mm 200 kN 200 mm gvz | 23x46 mm | DRX 200 | 745 mm | 348 mm  [stored 1.14173 ft] | 905 mm | galvanisch verzinkt | 200 mm | 12 mm  [stored 0.0393701 ft] | 1.350 mm | 200.00 kN | 813 mm |
| Doppel-Rollenlager, radial- axial  813-1350 DRX200 L= 200, roh | 150xrb121350 | 394 mm | MEFA Doppel-Rollenlager, radial- axial  813-1350 DRX200 L= 200 | 4250928436474 | 81.45 kg | 81.45 kg | 195 mm | 813 - 1.350 mm 200 kN 200 mm roh | 23x46 mm | DRX 200 | 745 mm | 348 mm  [stored 1.14173 ft] | 905 mm | roh | 200 mm | 8 mm  [stored 0.0262467 ft] | 1.350 mm | 200.00 kN | 813 mm |
| Doppel-Rollenlager, radial- axial  813-1350 DRX200 L= 300, fvz | 150xfc121350 | 394 mm | MEFA Doppel-Rollenlager, radial- axial  813-1350 DRX200 L= 300 | 4250928435828 | 84.64 kg | 84.64 kg | 195 mm | 813 - 1.350 mm 200 kN 300 mm fsv | 23x46 mm | DRX 200 | 845 mm | 348 mm  [stored 1.14173 ft] | 1005 mm | feuerstückverzinkt | 300 mm | 12 mm  [stored 0.0393701 ft] | 1.350 mm | 200.00 kN | 813 mm |
| Doppel-Rollenlager, radial- axial  813-1350 DRX200 L= 300, gvz | 150xgc121350 | 394 mm | MEFA Doppel-Rollenlager, radial- axial  813-1350 DRX200 L= 300 | 4250928436214 | 80.90 kg | 80.90 kg | 195 mm | 813 - 1.350 mm 200 kN 300 mm gvz | 23x46 mm | DRX 200 | 845 mm | 348 mm  [stored 1.14173 ft] | 1005 mm | galvanisch verzinkt | 300 mm | 12 mm  [stored 0.0393701 ft] | 1.350 mm | 200.00 kN | 813 mm |
| Doppel-Rollenlager, radial- axial  813-1350 DRX200 L= 300, roh | 150xrc121350 | 394 mm | MEFA Doppel-Rollenlager, radial- axial  813-1350 DRX200 L= 300 | 4250928436603 | 82.95 kg | 82.95 kg | 195 mm | 813 - 1.350 mm 200 kN 300 mm roh | 23x46 mm | DRX 200 | 845 mm | 348 mm  [stored 1.14173 ft] | 1005 mm | roh | 300 mm | 8 mm  [stored 0.0262467 ft] | 1.350 mm | 200.00 kN | 813 mm |
| Doppel-Rollenlager, radial- axial 1120-1920 DRX100 L= 100, fvz | 150xfa101920 | 438 mm | MEFA Doppel-Rollenlager, radial- axial 1120-1920 DRX100 L= 100 | 4250928435552 | 140.12 kg | 140.12 kg | 274 mm | 1120 - 1.920 mm 100 kN 100 mm fsv | 27x54 mm | DRX 100 | 870 mm | 384 mm  [stored 1.25984 ft] | 1030 mm | feuerstückverzinkt | 100 mm | 10 mm  [stored 0.0328084 ft] | 1.920 mm | 100.00 kN | 1.120 mm |
| Doppel-Rollenlager, radial- axial 1120-1920 DRX100 L= 100, gvz | 150xga101920 | 438 mm | MEFA Doppel-Rollenlager, radial- axial 1120-1920 DRX100 L= 100 | 4250928435941 | 137.63 kg | 137.63 kg | 274 mm | 1120 - 1.920 mm 100 kN 100 mm gvz | 27x54 mm | DRX 100 | 870 mm | 384 mm  [stored 1.25984 ft] | 1030 mm | galvanisch verzinkt | 100 mm | 10 mm  [stored 0.0328084 ft] | 1.920 mm | 100.00 kN | 1.120 mm |
| Doppel-Rollenlager, radial- axial 1120-1920 DRX100 L= 100, roh | 150xra101920 | 438 mm | MEFA Doppel-Rollenlager, radial- axial 1120-1920 DRX100 L= 100 | 4250928436337 | 137.63 kg | 137.63 kg | 274 mm | 1120 - 1.920 mm 100 kN 100 mm roh | 27x54 mm | DRX 100 | 870 mm | 384 mm  [stored 1.25984 ft] | 1030 mm | roh | 100 mm | 10 mm  [stored 0.0328084 ft] | 1.920 mm | 100.00 kN | 1.120 mm |
| Doppel-Rollenlager, radial- axial 1120-1920 DRX100 L= 200, fvz | 150xfb101920 | 438 mm | MEFA Doppel-Rollenlager, radial- axial 1120-1920 DRX100 L= 200 | 4250928435682 | 142.02 kg | 142.02 kg | 274 mm | 1120 - 1.920 mm 100 kN 200 mm fsv | 27x54 mm | DRX 100 | 970 mm | 384 mm  [stored 1.25984 ft] | 1130 mm | feuerstückverzinkt | 200 mm | 10 mm  [stored 0.0328084 ft] | 1.920 mm | 100.00 kN | 1.120 mm |
| Doppel-Rollenlager, radial- axial 1120-1920 DRX100 L= 200, gvz | 150xgb101920 | 438 mm | MEFA Doppel-Rollenlager, radial- axial 1120-1920 DRX100 L= 200 | 4250928436078 | 136.00 kg | 136.00 kg | 274 mm | 1120 - 1.920 mm 100 kN 200 mm gvz | 27x54 mm | DRX 100 | 970 mm | 384 mm  [stored 1.25984 ft] | 1130 mm | galvanisch verzinkt | 200 mm | 10 mm  [stored 0.0328084 ft] | 1.920 mm | 100.00 kN | 1.120 mm |
| Doppel-Rollenlager, radial- axial 1120-1920 DRX100 L= 200, roh | 150xrb101920 | 438 mm | MEFA Doppel-Rollenlager, radial- axial 1120-1920 DRX100 L= 200 | 4250928436467 | 139.44 kg | 139.44 kg | 274 mm | 1120 - 1.920 mm 100 kN 200 mm roh | 27x54 mm | DRX 100 | 970 mm | 384 mm  [stored 1.25984 ft] | 1130 mm | roh | 200 mm | 10 mm  [stored 0.0328084 ft] | 1.920 mm | 100.00 kN | 1.120 mm |
| Doppel-Rollenlager, radial- axial 1120-1920 DRX100 L= 300, fvz | 150xfc101920 | 438 mm | MEFA Doppel-Rollenlager, radial- axial 1120-1920 DRX100 L= 300 | 4250928435811 | 143.93 kg | 143.93 kg | 274 mm | 1120 - 1.920 mm 100 kN 300 mm fsv | 27x54 mm | DRX 100 | 1 mm  [stored 0.00328084 ft] | 384 mm  [stored 1.25984 ft] | 1230 mm | feuerstückverzinkt | 300 mm | 10 mm  [stored 0.0328084 ft] | 1.920 mm | 100.00 kN | 1.120 mm |
| Doppel-Rollenlager, radial- axial 1120-1920 DRX100 L= 300, gvz | 150xgc101920 | 438 mm | MEFA Doppel-Rollenlager, radial- axial 1120-1920 DRX100 L= 300 | 4250928436207 | 137.70 kg | 137.70 kg | 274 mm | 1120 - 1.920 mm 100 kN 300 mm gvz | 27x54 mm | DRX 100 | 1 mm  [stored 0.00328084 ft] | 384 mm  [stored 1.25984 ft] | 1230 mm | galvanisch verzinkt | 300 mm | 10 mm  [stored 0.0328084 ft] | 1.920 mm | 100.00 kN | 1.120 mm |
| Doppel-Rollenlager, radial- axial 1120-1920 DRX100 L= 300, roh | 150xrc101920 | 438 mm | MEFA Doppel-Rollenlager, radial- axial 1120-1920 DRX100 L= 300 | 4250928436597 | 141.26 kg | 141.26 kg | 274 mm | 1120 - 1.920 mm 100 kN 300 mm roh | 27x54 mm | DRX 100 | 1 mm  [stored 0.00328084 ft] | 384 mm  [stored 1.25984 ft] | 1230 mm | roh | 300 mm | 10 mm  [stored 0.0328084 ft] | 1.920 mm | 100.00 kN | 1.120 mm |
| Doppel-Rollenlager, radial- axial 1120-1920 DRX200 L= 100, fvz | 150xfa121920 | 442 mm | MEFA Doppel-Rollenlager, radial- axial 1120-1920 DRX200 L= 100 | 4250928435576 | 147.18 kg | 147.18 kg | 274 mm | 1120 - 1.920 mm 200 kN 100 mm fsv | 27x54 mm | DRX 200 | 870 mm | 388 mm  [stored 1.27297 ft] | 1030 mm | feuerstückverzinkt | 100 mm | 10 mm  [stored 0.0328084 ft] | 1.920 mm | 200.00 kN | 1.120 mm |
| Doppel-Rollenlager, radial- axial 1120-1920 DRX200 L= 100, roh | 150xra121920 | 442 mm | MEFA Doppel-Rollenlager, radial- axial 1120-1920 DRX200 L= 100 | 4250928436351 | 144.68 kg | 144.68 kg | 274 mm | 1120 - 1.920 mm 200 kN 100 mm roh | 27x54 mm | DRX 200 | 870 mm | 388 mm  [stored 1.27297 ft] | 1030 mm | roh | 100 mm | 10 mm  [stored 0.0328084 ft] | 1.920 mm | 200.00 kN | 1.120 mm |
| Doppel-Rollenlager, radial- axial 1120-1920 DRX200 L= 100, gvz | 150xga121920 | 442 mm | MEFA Doppel-Rollenlager, radial- axial 1120-1920 DRX200 L= 100 | 4250928435965 | 141.20 kg | 141.20 kg | 274 mm | 1120 - 1.920 mm 200 kN 100 mm gvz | 27x54 mm | DRX 200 | 870 mm | 388 mm  [stored 1.27297 ft] | 1030 mm | galvanisch verzinkt | 100 mm | 10 mm  [stored 0.0328084 ft] | 1.920 mm | 200.00 kN | 1.120 mm |
| Doppel-Rollenlager, radial- axial 1120-1920 DRX200 L= 200, fvz | 150xfb121920 | 442 mm | MEFA Doppel-Rollenlager, radial- axial 1120-1920 DRX200 L= 200 | 4250928435705 | 149.08 kg | 149.08 kg | 274 mm | 1120 - 1.920 mm 200 kN 200 mm fsv | 27x54 mm | DRX 200 | 970 mm | 388 mm  [stored 1.27297 ft] | 1130 mm | feuerstückverzinkt | 200 mm | 10 mm  [stored 0.0328084 ft] | 1.920 mm | 200.00 kN | 1.120 mm |
| Doppel-Rollenlager, radial- axial 1120-1920 DRX200 L= 200, gvz | 150xgb121920 | 442 mm | MEFA Doppel-Rollenlager, radial- axial 1120-1920 DRX200 L= 200 | 4250928436092 | 143.00 kg | 143.00 kg | 274 mm | 1120 - 1.920 mm 200 kN 200 mm gvz | 27x54 mm | DRX 200 | 970 mm | 388 mm  [stored 1.27297 ft] | 1130 mm | galvanisch verzinkt | 200 mm | 10 mm  [stored 0.0328084 ft] | 1.920 mm | 200.00 kN | 1.120 mm |
| Doppel-Rollenlager, radial- axial 1120-1920 DRX200 L= 200, roh | 150xrb121920 | 442 mm | MEFA Doppel-Rollenlager, radial- axial 1120-1920 DRX200 L= 200 | 4250928436481 | 146.50 kg | 146.50 kg | 274 mm | 1120 - 1.920 mm 200 kN 200 mm roh | 27x54 mm | DRX 200 | 970 mm | 388 mm  [stored 1.27297 ft] | 1130 mm | roh | 200 mm | 10 mm  [stored 0.0328084 ft] | 1.920 mm | 200.00 kN | 1.120 mm |
| Doppel-Rollenlager, radial- axial 1120-1920 DRX200 L= 300, fvz | 150xfc121920 | 442 mm | MEFA Doppel-Rollenlager, radial- axial 1120-1920 DRX200 L= 300 | 4250928435835 | 150.99 kg | 150.99 kg | 274 mm | 1120 - 1.920 mm 200 kN 300 mm fsv | 27x54 mm | DRX 200 | 1 mm  [stored 0.00328084 ft] | 388 mm  [stored 1.27297 ft] | 1230 mm | feuerstückverzinkt | 300 mm | 10 mm  [stored 0.0328084 ft] | 1.920 mm | 200.00 kN | 1.120 mm |
| Doppel-Rollenlager, radial- axial 1120-1920 DRX200 L= 300, gvz | 150xgc121920 | 442 mm | MEFA Doppel-Rollenlager, radial- axial 1120-1920 DRX200 L= 300 | 4250928436221 | 144.70 kg | 144.70 kg | 274 mm | 1120 - 1.920 mm 200 kN 300 mm gvz | 27x54 mm | DRX 200 | 1 mm  [stored 0.00328084 ft] | 388 mm  [stored 1.27297 ft] | 1230 mm | galvanisch verzinkt | 300 mm | 10 mm  [stored 0.0328084 ft] | 1.920 mm | 200.00 kN | 1.120 mm |
| Doppel-Rollenlager, radial- axial 1120-1920 DRX200 L= 300, roh | 150xrc121920 | 442 mm | MEFA Doppel-Rollenlager, radial- axial 1120-1920 DRX200 L= 300 | 4250928436610 | 148.32 kg | 148.32 kg | 274 mm | 1120 - 1.920 mm 200 kN 300 mm roh | 27x54 mm | DRX 200 | 1 mm  [stored 0.00328084 ft] | 388 mm  [stored 1.27297 ft] | 1230 mm | roh | 300 mm | 10 mm  [stored 0.0328084 ft] | 1.920 mm | 200.00 kN | 1.120 mm |
| Doppel-Rollenlager, radial- axial 1120-1920 DRX300 L= 100, fvz | 150xfa151920 | 448 mm | MEFA Doppel-Rollenlager, radial- axial 1120-1920 DRX300 L= 100 | 4250928435583 | 157.89 kg | 157.89 kg | 274 mm | 1120 - 1.920 mm 300 kN 100 mm fsv | 27x54 mm | DRX 300 | 870 mm | 394 mm | 1030 mm | feuerstückverzinkt | 100 mm | 10 mm  [stored 0.0328084 ft] | 1.920 mm | 300.00 kN | 1.120 mm |
| Doppel-Rollenlager, radial- axial 1120-1920 DRX300 L= 100, gvz | 150xga151920 | 448 mm | MEFA Doppel-Rollenlager, radial- axial 1120-1920 DRX300 L= 100 | 4250928435972 | 151.70 kg | 151.70 kg | 274 mm | 1120 - 1.920 mm 300 kN 100 mm gvz | 27x54 mm | DRX 300 | 870 mm | 394 mm | 1030 mm | galvanisch verzinkt | 100 mm | 10 mm  [stored 0.0328084 ft] | 1.920 mm | 300.00 kN | 1.120 mm |
| Doppel-Rollenlager, radial- axial 1120-1920 DRX300 L= 100, roh | 150xra151920 | 448 mm | MEFA Doppel-Rollenlager, radial- axial 1120-1920 DRX300 L= 100 | 4250928436368 | 155.39 kg | 155.39 kg | 274 mm | 1120 - 1.920 mm 300 kN 100 mm roh | 27x54 mm | DRX 300 | 870 mm | 394 mm | 1030 mm | roh | 100 mm | 12 mm  [stored 0.0393701 ft] | 1.920 mm | 300.00 kN | 1.120 mm |
| Doppel-Rollenlager, radial- axial 1120-1920 DRX300 L= 200, fvz | 150xfb151920 | 448 mm | MEFA Doppel-Rollenlager, radial- axial 1120-1920 DRX300 L= 200 | 4250928435712 | 159.80 kg | 159.80 kg | 274 mm | 1120 - 1.920 mm 300 kN 200 mm fsv | 27x54 mm | DRX 300 | 970 mm | 394 mm | 1130 mm | feuerstückverzinkt | 200 mm | 10 mm  [stored 0.0328084 ft] | 1.920 mm | 300.00 kN | 1.120 mm |
| Doppel-Rollenlager, radial- axial 1120-1920 DRX300 L= 200, gvz | 150xgb151920 | 448 mm | MEFA Doppel-Rollenlager, radial- axial 1120-1920 DRX300 L= 200 | 4250928436108 | 153.40 kg | 153.40 kg | 274 mm | 1120 - 1.920 mm 300 kN 200 mm gvz | 27x54 mm | DRX 300 | 970 mm | 394 mm | 1130 mm | galvanisch verzinkt | 200 mm | 10 mm  [stored 0.0328084 ft] | 1.920 mm | 300.00 kN | 1.120 mm |
| Doppel-Rollenlager, radial- axial 1120-1920 DRX300 L= 200, roh | 150xrb151920 | 448 mm | MEFA Doppel-Rollenlager, radial- axial 1120-1920 DRX300 L= 200 | 4250928436498 | 157.20 kg | 157.20 kg | 274 mm | 1120 - 1.920 mm 300 kN 200 mm roh | 27x54 mm | DRX 300 | 970 mm | 394 mm | 1130 mm | roh | 200 mm | 15 mm  [stored 0.0492126 ft] | 1.920 mm | 300.00 kN | 1.120 mm |
| Doppel-Rollenlager, radial- axial 1120-1920 DRX300 L= 300, fvz | 150xfc151920 | 448 mm | MEFA Doppel-Rollenlager, radial- axial 1120-1920 DRX300 L= 300 | 4250928435842 | 161.70 kg | 161.70 kg | 274 mm | 1120 - 1.920 mm 300 kN 300 mm fsv | 27x54 mm | DRX 300 | 1 mm  [stored 0.00328084 ft] | 394 mm | 1230 mm | feuerstückverzinkt | 300 mm | 10 mm  [stored 0.0328084 ft] | 1.920 mm | 300.00 kN | 1.120 mm |
| Doppel-Rollenlager, radial- axial 1120-1920 DRX300 L= 300, gvz | 150xgc151920 | 448 mm | MEFA Doppel-Rollenlager, radial- axial 1120-1920 DRX300 L= 300 | 4250928436238 | 155.10 kg | 155.10 kg | 274 mm | 1120 - 1.920 mm 300 kN 300 mm gvz | 27x54 mm | DRX 300 | 1 mm  [stored 0.00328084 ft] | 394 mm | 1230 mm | galvanisch verzinkt | 300 mm | 10 mm  [stored 0.0328084 ft] | 1.920 mm | 300.00 kN | 1.120 mm |
| Doppel-Rollenlager, radial- axial 1120-1920 DRX300 L= 300, roh | 150xrc151920 | 448 mm | MEFA Doppel-Rollenlager, radial- axial 1120-1920 DRX300 L= 300 | 4250928436627 | 159.02 kg | 159.02 kg | 274 mm | 1120 - 1.920 mm 300 kN 300 mm roh | 27x54 mm | DRX 300 | 1 mm  [stored 0.00328084 ft] | 394 mm | 1230 mm | roh | 300 mm | 10 mm  [stored 0.0328084 ft] | 1.920 mm | 300.00 kN | 1.120 mm |

note: [stored X ft] marks values corroborated as IEEE doubles in the binary element streams (Revit-internal decimal feet)
